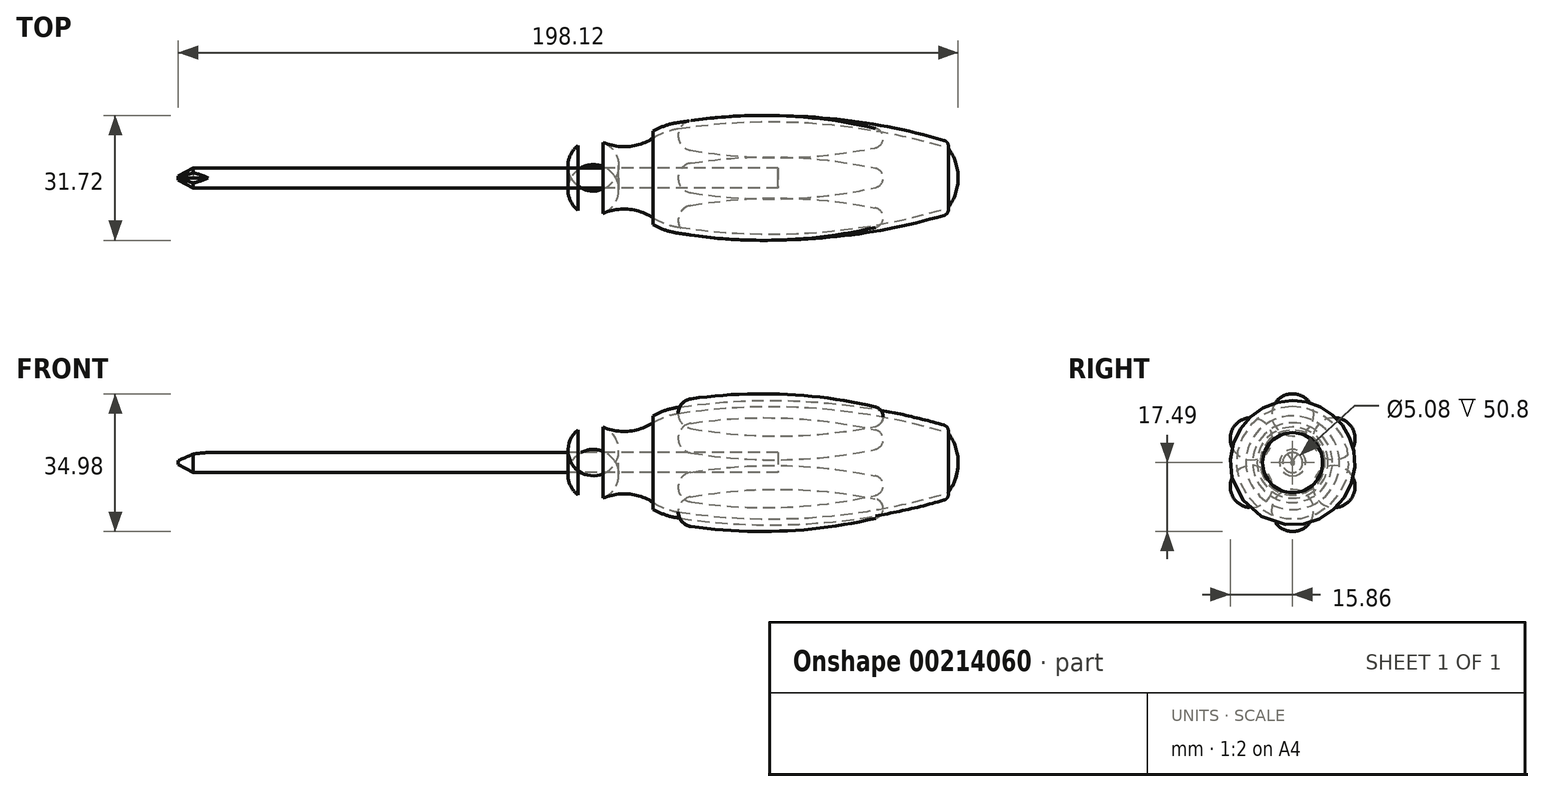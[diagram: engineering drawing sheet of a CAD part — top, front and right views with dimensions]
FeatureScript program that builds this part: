
annotation { "Feature Type Name" : "Feature", "Feature Type Description" : "" }
export const myFeature = defineFeature(function(context is Context, id is Id, definition is map)
    precondition{}
    {
        {
            var Q0;
            Q0=qCreatedBy(makeId("Front.planeOp"),FACE);
            var sketch = newSketch(context, id + "F0", { "sketchPlane" : qUnion([Q0])});
            skLineSegment(sketch, "E0", {"start": v(-101.6, 0) * mm, "end": v(96.52, 0) * mm});
            skLineSegment(sketch, "E1", {"start": v(96.52, 0) * mm, "end": v(117.55, 0) * mm, "construction": true});
            skLineSegment(sketch, "E2", {"start": v(50.8, 2.54) * mm, "end": v(-97.8, 2.54) * mm});
            skLineSegment(sketch, "E3", {"start": v(-101.6, 0.5) * mm, "end": v(-101.6, 0) * mm});
            skLineSegment(sketch, "E4", {"start": v(0, 2.54) * mm, "end": v(0, 8.25) * mm});
            skArc(sketch, "E5", {"start": v(6.35, 9.02) * mm, "mid": v(3.07, 9.48) * mm, "end": v(0, 8.25) * mm});
            skArc(sketch, "E6", {"start": v(6.35, 9.02) * mm, "mid": v(12.84, 7.99) * mm, "end": v(19.05, 10.11) * mm});
            skArc(sketch, "E7", {"start": v(25.4, 12.52) * mm, "mid": v(22.1, 11.65) * mm, "end": v(19.05, 10.11) * mm});
            skArc(sketch, "E8", {"start": v(93.98, 7.62) * mm, "mid": v(59.96, 13.9) * mm, "end": v(25.4, 12.52) * mm});
            skArc(sketch, "E9", {"start": v(96.52, 0) * mm, "mid": v(95.87, 4.02) * mm, "end": v(93.98, 7.62) * mm});
            skArc(sketch, "E10.0", {"start": v(25.17, 14.02) * mm, "mid": v(22.01, 13.24) * mm, "end": v(19.05, 11.9) * mm});
            skArc(sketch, "E10.1", {"start": v(92.95, 9.52) * mm, "mid": v(59.3, 15.46) * mm, "end": v(25.17, 14.02) * mm});
            skLineSegment(sketch, "E11", {"start": v(19.05, 11.9) * mm, "end": v(19.05, 10.11) * mm});
            skArc(sketch, "E12", {"start": v(93.98, 7.62) * mm, "mid": v(93.86, 8.78) * mm, "end": v(92.95, 9.52) * mm});
            skPoint(sketch, "E13.orphan", {"position": v(0, 0) * mm});
            skLineSegment(sketch, "E14", {"start": v(50.8, 2.54) * mm, "end": v(50.8, 0) * mm});
            skLineSegment(sketch, "E15", {"start": v(-101.6, 0.5) * mm, "end": v(-97.8, 2.54) * mm});
            skPoint(sketch, "E16.orphan", {"position": v(-101.6, 2.54) * mm});
            skSolve(sketch);
        }
        {
            var Q0;
            Q0=qCreatedBy(makeId("Front.planeOp"),FACE);
            var sketch = newSketch(context, id + "F1", { "sketchPlane" : qUnion([Q0])});
            skLineSegment(sketch, "E17", {"start": v(25.4, 12.52) * mm, "end": v(77.47, 11.64) * mm});
            skArc(sketch, "E18", {"start": v(28.67, 16.22) * mm, "mid": v(26.35, 14.97) * mm, "end": v(25.4, 12.52) * mm});
            skArc(sketch, "E19", {"start": v(77.47, 11.64) * mm, "mid": v(76.93, 13.25) * mm, "end": v(75.5, 14.16) * mm});
            skArc(sketch, "E20", {"start": v(75.5, 14.16) * mm, "mid": v(52.19, 17.37) * mm, "end": v(28.67, 16.22) * mm});
            skSolve(sketch);
        }
        {
            var Q0;
            Q0=qCreatedBy(makeId("Front.planeOp"),FACE);
            var sketch = newSketch(context, id + "F2", { "sketchPlane" : qUnion([Q0])});
            skLineSegment(sketch, "E21", {"start": v(-101.6, 0.5) * mm, "end": v(-93.98, 2.54) * mm});
            skSolve(sketch);
        }
        {
            var Q0;
            Q0=sQuery(id+"F2.wireOp",VERTEX,"E21.start");
            var Q1;
            Q1=sQuery(id+"F2.wireOp",EDGE,"E21");
            cPlane(context, id + "F3", {"entities" : qUnion([Q0, Q1]), "cplaneType" : CPlaneType.LINE_POINT, "offset" : 25.4 * mm, "width" : 152.4 * mm, "height" : 152.4 * mm});
        }
        {
            var Q0;
            Q0=qCreatedBy(id+"F3.planeOp",FACE);
            var sketch = newSketch(context, id + "F4", { "sketchPlane" : qUnion([Q0])});
            skLineSegment(sketch, "E22", {"start": v(5.08, 29.2) * mm, "end": v(0, 26.67) * mm});
            skLineSegment(sketch, "E23", {"start": v(0, 26.67) * mm, "end": v(-5.08, 29.2) * mm});
            skLineSegment(sketch, "E24", {"start": v(-5.08, 29.2) * mm, "end": v(5.08, 29.2) * mm});
            skLineSegment(sketch, "E25", {"start": v(0, 29.2) * mm, "end": v(0, 26.67) * mm, "construction": true});
            skSolve(sketch);
        }
        {
            var Q0;
            {var subQ0=sQuery(id+"F0.wireOp",EDGE,"E3");Q0=makeQuery(id+"F0.imprint","IMPRINT",FACE,{"disambiguationData":[TD([[makeQuery(id+"F0.imprint","IMPRINT",EDGE,{"derivedFrom":subQ0}),1.0]])]});}
            var Q1;
            Q1=sQuery(id+"F0.wireOp",EDGE,"E1");
            revolve(context, id + "F5", {"entities" : qUnion([Q0]), "axis" : qUnion([Q1]), "revolveType" : RevolveType.FULL});
        }
        {
            var Q0;
            {var subQ0=sQuery(id+"F0.wireOp",EDGE,"E4");Q0=makeQuery(id+"F0.imprint","IMPRINT",FACE,{"disambiguationData":[TD([[makeQuery(id+"F0.imprint","IMPRINT",EDGE,{"derivedFrom":subQ0}),-1.0]])]});}
            var Q1;
            Q1=sQuery(id+"F0.wireOp",EDGE,"E1");
            revolve(context, id + "F6", {"entities" : qUnion([Q0]), "axis" : qUnion([Q1]), "revolveType" : RevolveType.FULL});
        }
        {
            var Q0;
            Q0=makeQuery(id+"F0.imprint","IMPRINT",FACE,{"disambiguationData":[TD([[makeQuery(id+"F0.imprint","IMPRINT",EDGE,{"derivedFrom":sQuery(id+"F0.wireOp",EDGE,"E7")}),-1.0]])]});
            var Q1;
            Q1=sQuery(id+"F0.wireOp",EDGE,"E1");
            revolve(context, id + "F7", {"entities" : qUnion([Q0]), "axis" : qUnion([Q1]), "revolveType" : RevolveType.FULL});
        }
        {
            var Q0;
            Q0=makeQuery(id+"F1.imprint","IMPRINT",FACE,{"disambiguationData":[TD([[makeQuery(id+"F1.imprint","IMPRINT",EDGE,{"derivedFrom":sQuery(id+"F1.wireOp",EDGE,"E17")}),1.0]])]});
            var Q1;
            Q1=sQuery(id+"F1.wireOp",EDGE,"E17");
            revolve(context, id + "F8", {"entities" : qUnion([Q0]), "axis" : qUnion([Q1]), "revolveType" : RevolveType.FULL});
        }
        {
            var Q0;
            Q0=makeQuery(id+"F8.opRevolve","SWEPT_BODY",BODY,{"disambiguationData":[OSD([sQuery(id+"F1.wireOp",EDGE,"E17"),sQuery(id+"F1.wireOp",EDGE,"E18"),sQuery(id+"F1.wireOp",EDGE,"E19"),sQuery(id+"F1.wireOp",EDGE,"E20")])]});
            var Q1;
            Q1=sQuery(id+"F0.wireOp",EDGE,"E1");
            circularPattern(context, id + "F9", {"entities" : qUnion([Q0]), "axis" : qUnion([Q1]), "angle" : 360 * degree, "instanceCount" : 6, "equalSpace" : true});
        }
        {
            var Q0;
            Q0=makeQuery(id+"F6.opRevolve","SWEPT_BODY",BODY,{"disambiguationData":[OSD([sQuery(id+"F0.wireOp",EDGE,"E0"),sQuery(id+"F0.wireOp",EDGE,"E2"),sQuery(id+"F0.wireOp",EDGE,"E4"),sQuery(id+"F0.wireOp",EDGE,"E5"),sQuery(id+"F0.wireOp",EDGE,"E6"),sQuery(id+"F0.wireOp",EDGE,"E7"),sQuery(id+"F0.wireOp",EDGE,"E8"),sQuery(id+"F0.wireOp",EDGE,"E9"),sQuery(id+"F0.wireOp",EDGE,"E14")])]});
            var Q1;
            Q1=makeQuery(id+"F7.opRevolve","SWEPT_BODY",BODY,{"disambiguationData":[OSD([sQuery(id+"F0.wireOp",EDGE,"E7"),sQuery(id+"F0.wireOp",EDGE,"E8"),sQuery(id+"F0.wireOp",EDGE,"E10.0"),sQuery(id+"F0.wireOp",EDGE,"E10.1"),sQuery(id+"F0.wireOp",EDGE,"E11"),sQuery(id+"F0.wireOp",EDGE,"E12")])]});
            booleanBodies(context, id + "F10", {"operationType" : BooleanOperationType.SUBTRACTION, "tools" : qUnion([Q0]), "targets" : qUnion([Q1]), "keepTools" : true});
        }
        {
            var Q0;
            Q0 = qSketchRegion(id + "F4", true);
            var Q1;
            Q1 = qConstructionFilter(qBodyType(qCreatedBy(id + "F2" ,EDGE), BodyType.WIRE), ConstructionObject.NO);
            sweep(context, id + "F11", {"operationType" : NewBodyOperationType.REMOVE, "profiles" : qUnion([Q0]), "path" : qUnion([Q1])});
        }
    });
